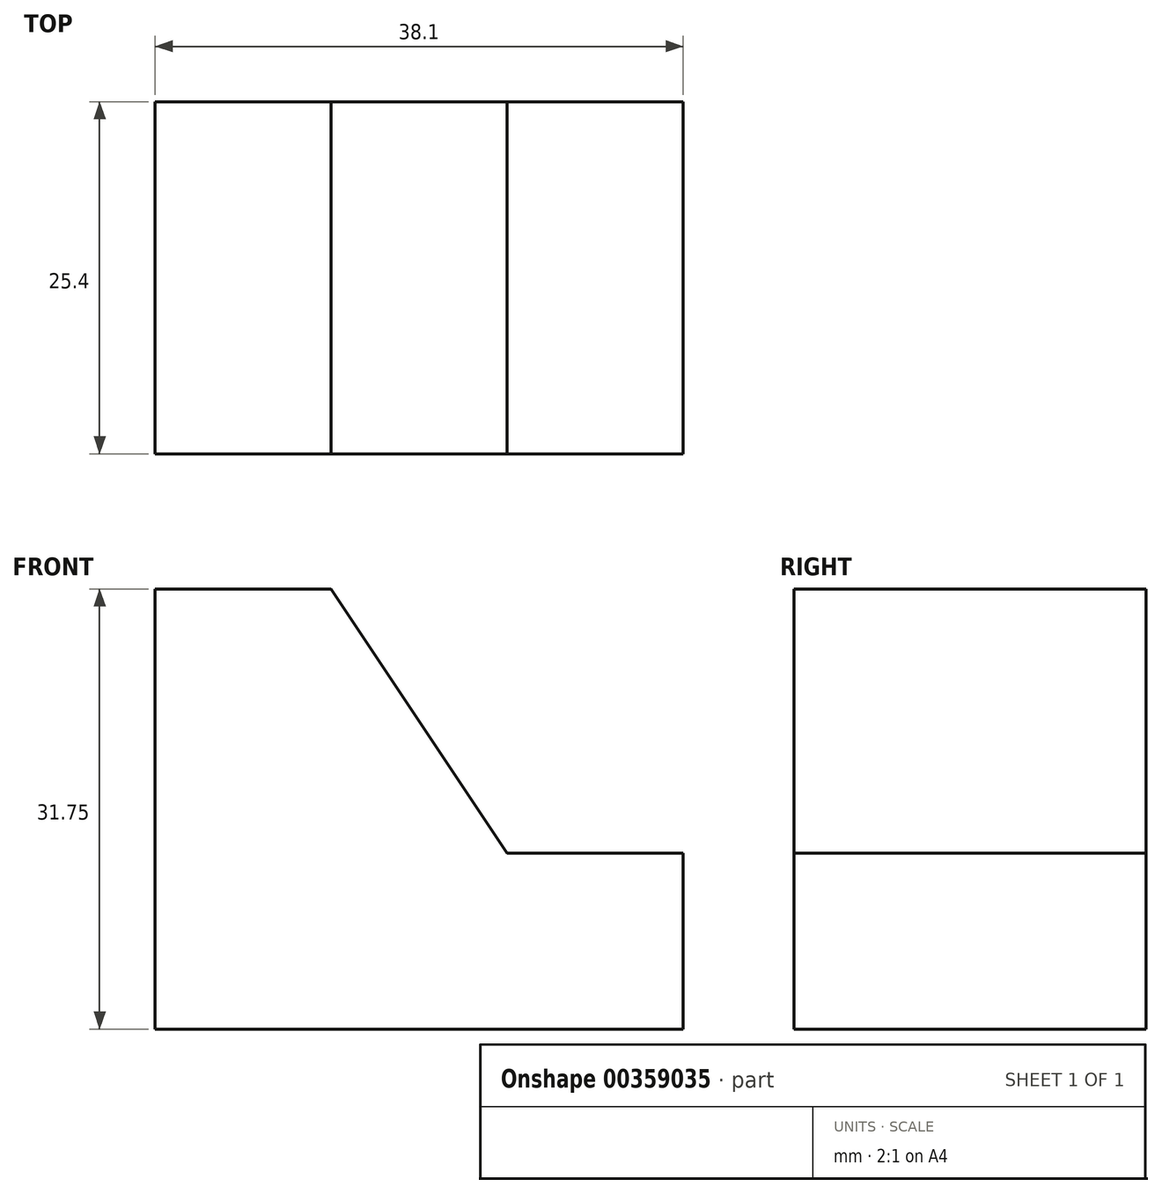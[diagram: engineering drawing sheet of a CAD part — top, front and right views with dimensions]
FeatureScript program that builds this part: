
annotation { "Feature Type Name" : "Feature", "Feature Type Description" : "" }
export const myFeature = defineFeature(function(context is Context, id is Id, definition is map)
    precondition{}
    {
        {
            var Q0;
            Q0=qCreatedBy(makeId("Front.planeOp"),FACE);
            var sketch = newSketch(context, id + "F0", { "sketchPlane" : qUnion([Q0])});
            skLineSegment(sketch, "E0", {"start": v(0, 0) * mm, "end": v(0, 31.75) * mm});
            skLineSegment(sketch, "E1", {"start": v(0, 31.75) * mm, "end": v(12.7, 31.75) * mm});
            skLineSegment(sketch, "E2", {"start": v(12.7, 31.75) * mm, "end": v(25.4, 12.7) * mm});
            skLineSegment(sketch, "E3", {"start": v(25.4, 12.7) * mm, "end": v(38.1, 12.7) * mm});
            skLineSegment(sketch, "E4", {"start": v(38.1, 12.7) * mm, "end": v(38.1, 0) * mm});
            skLineSegment(sketch, "E5", {"start": v(38.1, 0) * mm, "end": v(0, 0) * mm});
            skSolve(sketch);
        }
        {
            var Q0;
            Q0=makeQuery(id+"F0.imprint","IMPRINT",FACE,{"disambiguationData":[TD([[makeQuery(id+"F0.imprint","IMPRINT",EDGE,{"derivedFrom":sQuery(id+"F0.wireOp",EDGE,"E0")}),-1.0]])]});
            extrude(context, id + "F1", {"entities" : qUnion([Q0]), "oppositeDirection" : true, "depth" : 25.4 * mm});
        }
    });
